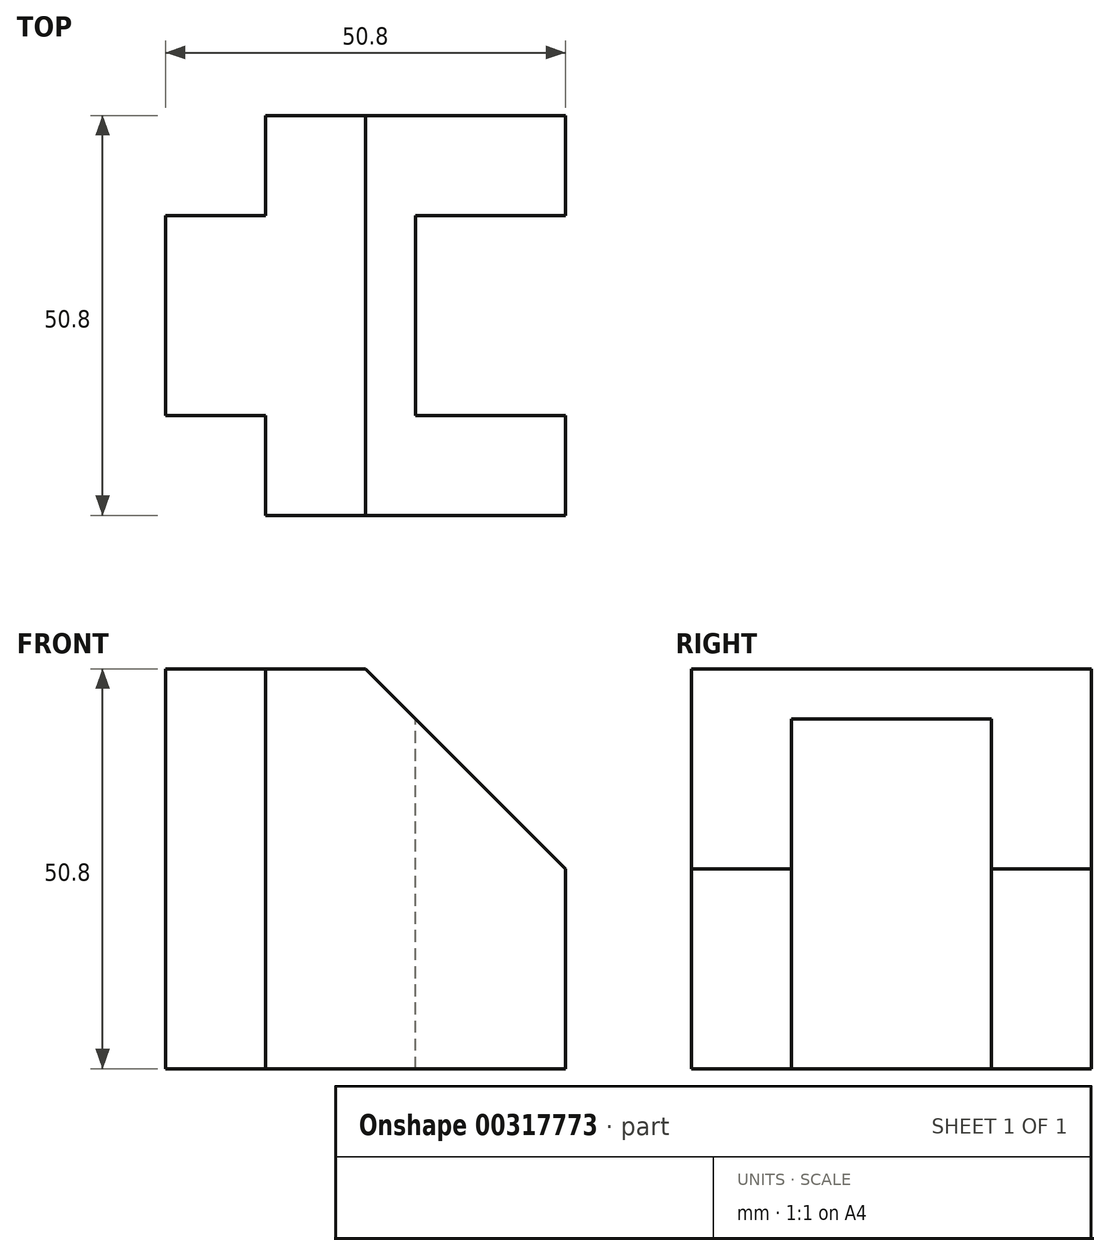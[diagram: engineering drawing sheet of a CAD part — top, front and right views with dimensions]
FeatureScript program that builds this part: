
annotation { "Feature Type Name" : "Feature", "Feature Type Description" : "" }
export const myFeature = defineFeature(function(context is Context, id is Id, definition is map)
    precondition{}
    {
        {
            var Q0;
            Q0=qCreatedBy(makeId("Front.planeOp"),FACE);
            var sketch = newSketch(context, id + "F0", { "sketchPlane" : qUnion([Q0])});
            skLineSegment(sketch, "E0", {"start": v(0, 0) * mm, "end": v(25.4, 0) * mm});
            skLineSegment(sketch, "E1", {"start": v(25.4, 0) * mm, "end": v(50.8, -25.4) * mm});
            skLineSegment(sketch, "E2", {"start": v(50.8, -25.4) * mm, "end": v(50.8, -50.8) * mm});
            skLineSegment(sketch, "E3", {"start": v(50.8, -50.8) * mm, "end": v(0, -50.8) * mm});
            skLineSegment(sketch, "E4", {"start": v(0, -50.8) * mm, "end": v(0, 0) * mm});
            skSolve(sketch);
        }
        {
            var Q0;
            Q0 = qSketchRegion(id + "F0", true);
            extrude(context, id + "F1", {"entities" : qUnion([Q0]), "depth" : 50.8 * mm});
        }
        {
            var Q0;
            Q0=makeQuery(id+"F1.opExtrude","SWEPT_FACE",FACE,{"disambiguationData":[OSD([sQuery(id+"F0.wireOp",EDGE,"E0")])]});
            var sketch = newSketch(context, id + "F2", { "sketchPlane" : qUnion([Q0])});
            skLineSegment(sketch, "E5.bottom", {"start": v(0, 0) * mm, "end": v(12.7, 0) * mm});
            skLineSegment(sketch, "E5.top", {"start": v(0, -12.7) * mm, "end": v(12.7, -12.7) * mm});
            skLineSegment(sketch, "E5.left", {"start": v(0, 0) * mm, "end": v(0, -12.7) * mm});
            skLineSegment(sketch, "E5.right", {"start": v(12.7, 0) * mm, "end": v(12.7, -12.7) * mm});
            skLineSegment(sketch, "E6.bottom", {"start": v(0, -50.8) * mm, "end": v(12.7, -50.8) * mm});
            skLineSegment(sketch, "E6.top", {"start": v(0, -38.1) * mm, "end": v(12.7, -38.1) * mm});
            skLineSegment(sketch, "E6.left", {"start": v(0, -50.8) * mm, "end": v(0, -38.1) * mm});
            skLineSegment(sketch, "E6.right", {"start": v(12.7, -50.8) * mm, "end": v(12.7, -38.1) * mm});
            skLineSegment(sketch, "E7.bottom", {"start": v(50.8, -12.7) * mm, "end": v(31.75, -12.7) * mm});
            skLineSegment(sketch, "E7.top", {"start": v(50.8, -38.1) * mm, "end": v(31.75, -38.1) * mm});
            skLineSegment(sketch, "E7.left", {"start": v(50.8, -12.7) * mm, "end": v(50.8, -38.1) * mm});
            skLineSegment(sketch, "E7.right", {"start": v(31.75, -12.7) * mm, "end": v(31.75, -38.1) * mm});
            skSolve(sketch);
        }
        {
            var Q0;
            Q0 = qSketchRegion(id + "F2", true);
            extrude(context, id + "F3", {"entities" : qUnion([Q0]), "operationType" : NewBodyOperationType.REMOVE, "endBound" : BoundingType.THROUGH_ALL, "oppositeDirection" : true, "depth" : 25.4 * mm});
        }
    });
